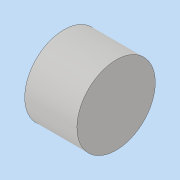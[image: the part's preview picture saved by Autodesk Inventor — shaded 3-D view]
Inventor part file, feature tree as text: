
AUTODESK INVENTOR PART (.ipt)
format: ipt  version: 2019 (Build 230136000, 136)  size: 122,880 bytes
history: native  units: mm
features: other x3, extrude x1, sketch x1
ambient origin geometry x8: Origin, YZ Plane, XZ Plane, XY Plane, X Axis, Y Axis, Z Axis, Center Point
bodies: Body1 (feature_tree)
feature tree (5):
  other  "Твердое тело1"
  extrude  "Выдавливание1"  Depth=30.0mm
  other  "Параллельный шлиц1"
  sketch  "Эскиз1"
  other  "Канавка вала"
